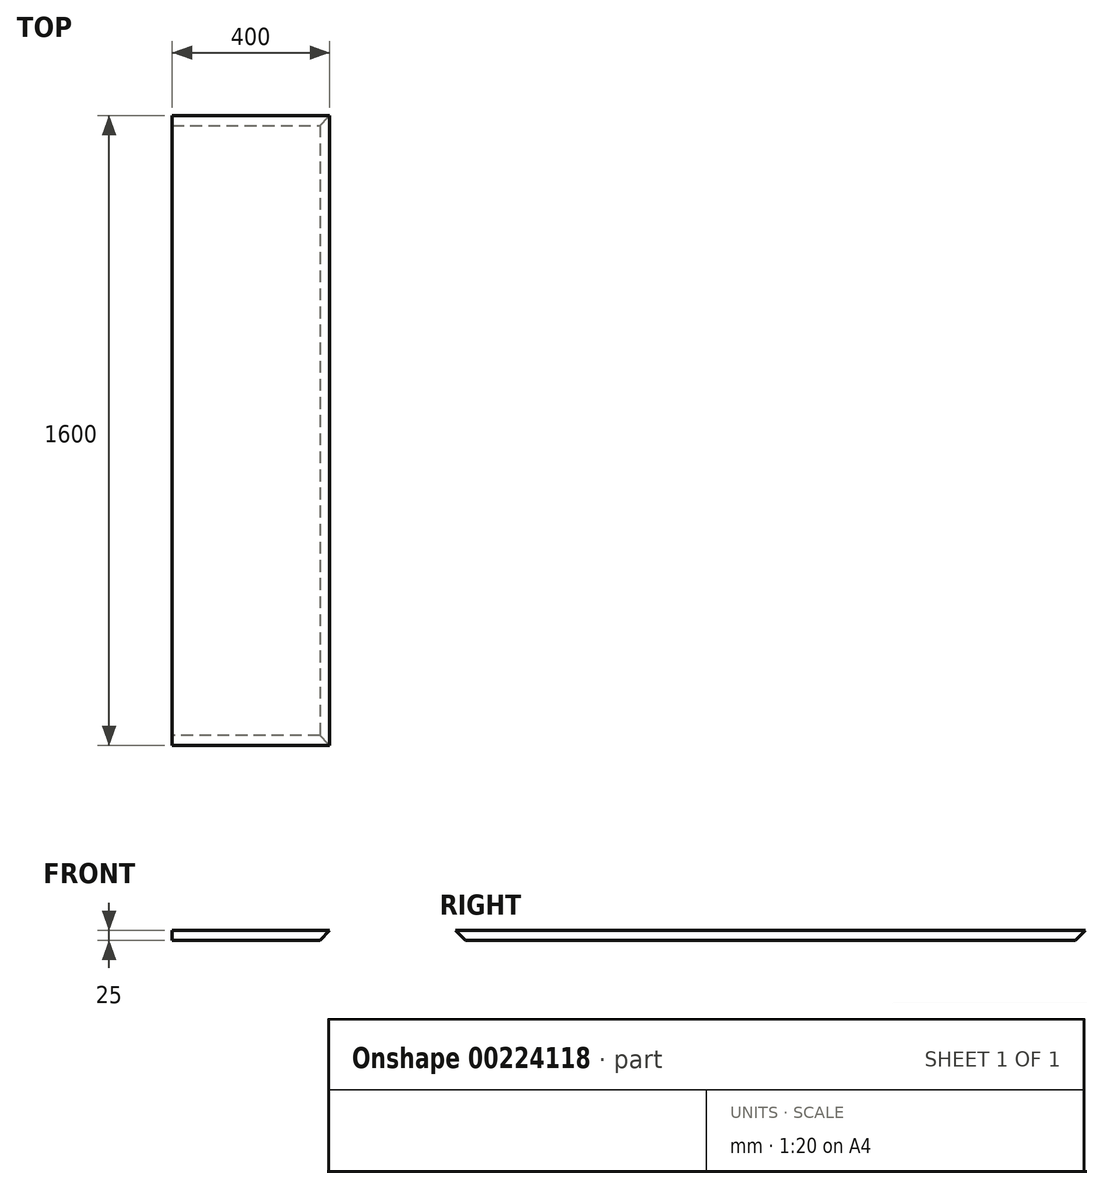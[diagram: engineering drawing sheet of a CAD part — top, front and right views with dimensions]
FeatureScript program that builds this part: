
annotation { "Feature Type Name" : "Feature", "Feature Type Description" : "" }
export const myFeature = defineFeature(function(context is Context, id is Id, definition is map)
    precondition{}
    {
        {
            var Q0;
            Q0=qCreatedBy(makeId("Top.planeOp"),FACE);
            var sketch = newSketch(context, id + "F0", { "sketchPlane" : qUnion([Q0])});
            skLineSegment(sketch, "E0.bottom", {"start": v(-200, 800) * mm, "end": v(200, 800) * mm});
            skLineSegment(sketch, "E0.top", {"start": v(-200, -800) * mm, "end": v(200, -800) * mm});
            skLineSegment(sketch, "E0.left", {"start": v(-200, 800) * mm, "end": v(-200, -800) * mm});
            skLineSegment(sketch, "E0.right", {"start": v(200, 800) * mm, "end": v(200, -800) * mm});
            skLineSegment(sketch, "E1", {"start": v(0, 800) * mm, "end": v(0, -800) * mm, "construction": true});
            skPoint(sketch, "E2.startSnap0", {"position": v(-200, 0) * mm});
            skLineSegment(sketch, "E3", {"start": v(-200, 0) * mm, "end": v(200, 0) * mm, "construction": true});
            skSolve(sketch);
        }
        {
            var Q0;
            Q0=makeQuery(id+"F0.imprint","IMPRINT",FACE,{"disambiguationData":[TD([[makeQuery(id+"F0.imprint","IMPRINT",EDGE,{"derivedFrom":sQuery(id+"F0.wireOp",EDGE,"E0.bottom")}),-1.0]])]});
            extrude(context, id + "F1", {"entities" : qUnion([Q0]), "endBound" : BoundingType.SYMMETRIC, "depth" : 25 * mm});
        }
        {
            var Q0;
            Q0=makeQuery(id+"F1.opExtrude","CAP_EDGE",EDGE,{"disambiguationData":[OSD([sQuery(id+"F0.wireOp",EDGE,"E0.top")])],"isStart":true});
            var Q1;
            Q1=makeQuery(id+"F1.opExtrude","CAP_EDGE",EDGE,{"disambiguationData":[OSD([sQuery(id+"F0.wireOp",EDGE,"E0.bottom")])],"isStart":true});
            var Q2;
            Q2=makeQuery(id+"F1.opExtrude","CAP_EDGE",EDGE,{"disambiguationData":[OSD([sQuery(id+"F0.wireOp",EDGE,"E0.right")])],"isStart":true});
            chamfer(context, id + "F2", {"entities" : qUnion([Q0, Q1, Q2]), "width" : 25 * mm, "tangentPropagation" : true});
        }
    });
